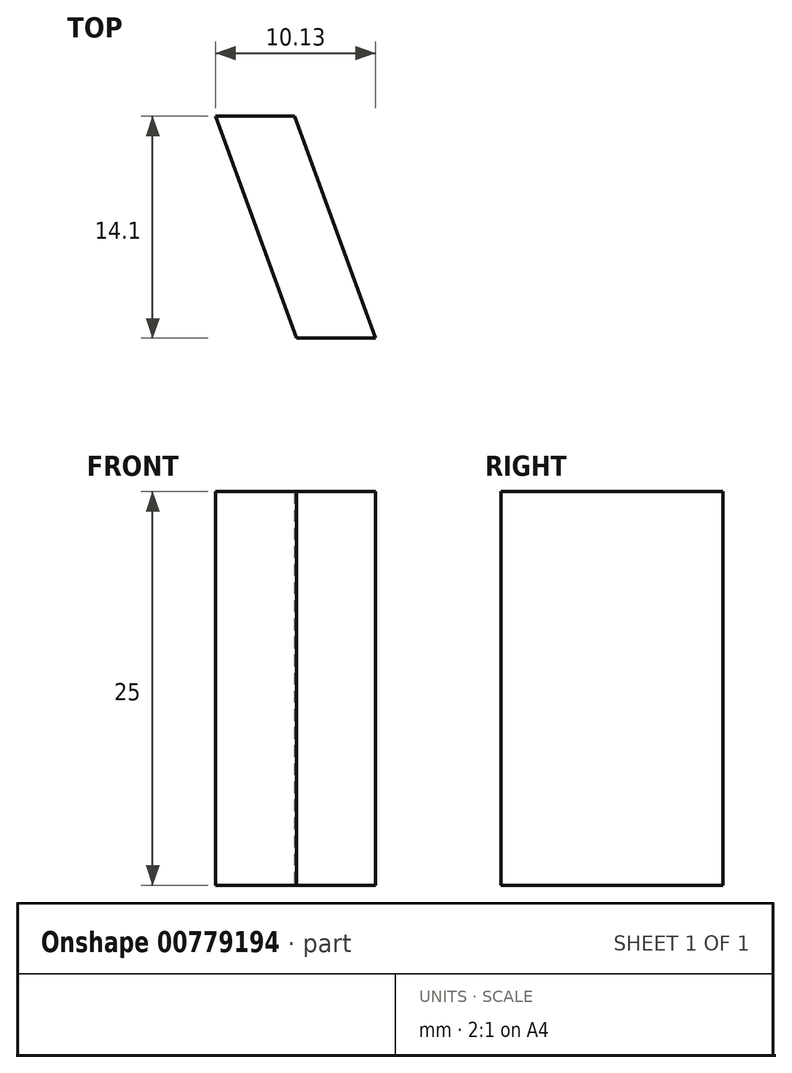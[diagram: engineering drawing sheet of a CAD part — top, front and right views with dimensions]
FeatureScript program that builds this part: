
annotation { "Feature Type Name" : "Feature", "Feature Type Description" : "" }
export const myFeature = defineFeature(function(context is Context, id is Id, definition is map)
    precondition{}
    {
        {
            var Q0;
            Q0=qCreatedBy(makeId("Top.planeOp"),FACE);
            var sketch = newSketch(context, id + "F0", { "sketchPlane" : qUnion([Q0])});
            skLineSegment(sketch, "E0", {"start": v(0, 0) * mm, "end": v(-5.13, 14.1) * mm});
            skLineSegment(sketch, "E1", {"start": v(0, 0) * mm, "end": v(-5, 0) * mm});
            skLineSegment(sketch, "E2", {"start": v(-5.13, 14.1) * mm, "end": v(-10.13, 14.1) * mm});
            skLineSegment(sketch, "E3", {"start": v(-10.13, 14.1) * mm, "end": v(-5, 0) * mm});
            skSolve(sketch);
        }
        {
            var Q0;
            Q0=qSketchRegion(id+"F0",true);
            extrude(context, id + "F1", {"entities" : qUnion([Q0]), "depth" : 25 * mm});
        }
    });
